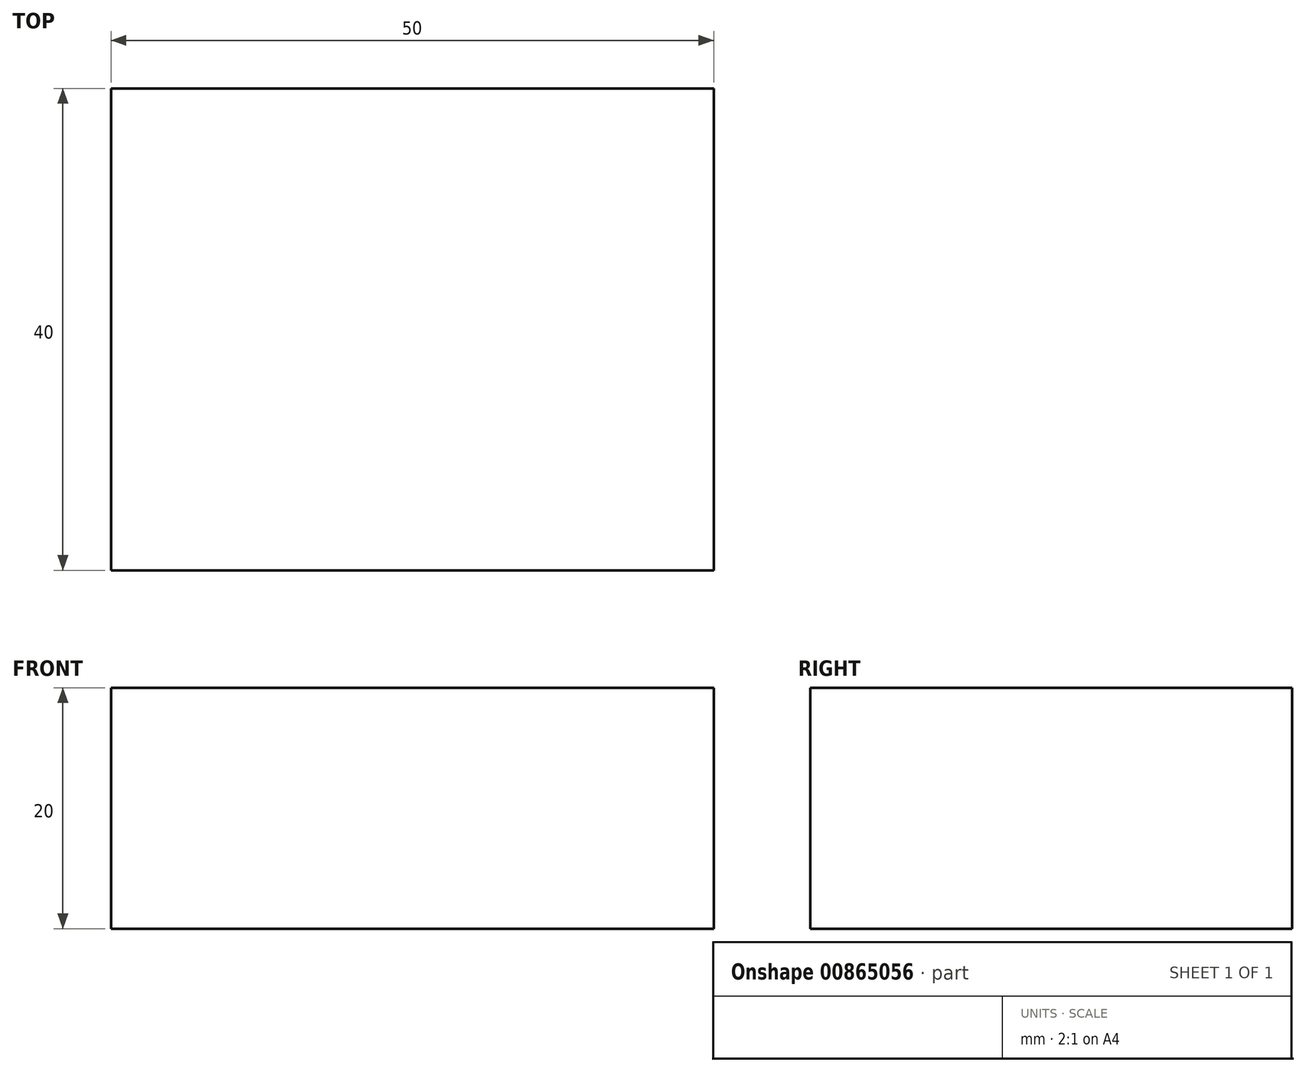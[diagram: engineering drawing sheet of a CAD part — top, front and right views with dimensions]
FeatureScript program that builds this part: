
annotation { "Feature Type Name" : "Feature", "Feature Type Description" : "" }
export const myFeature = defineFeature(function(context is Context, id is Id, definition is map)
    precondition{}
    {
        {
            var Q0;
            Q0=qCreatedBy(makeId("Front.planeOp"),FACE);
            var sketch = newSketch(context, id + "F0", { "sketchPlane" : qUnion([Q0])});
            skLineSegment(sketch, "E0.bottom", {"start": v(0, 0) * mm, "end": v(50, 0) * mm});
            skLineSegment(sketch, "E0.top", {"start": v(0, 20) * mm, "end": v(50, 20) * mm});
            skLineSegment(sketch, "E0.left", {"start": v(0, 0) * mm, "end": v(0, 20) * mm});
            skLineSegment(sketch, "E0.right", {"start": v(50, 0) * mm, "end": v(50, 20) * mm});
            skSolve(sketch);
        }
        {
            var Q0;
            Q0 = qSketchRegion(id + "F0", true);
            extrude(context, id + "F1", {"entities" : qUnion([Q0]), "depth" : 40 * mm, "offsetDistance" : 25 * mm});
        }
    });
